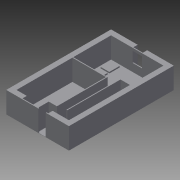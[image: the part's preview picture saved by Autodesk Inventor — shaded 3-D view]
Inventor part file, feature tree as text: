
AUTODESK INVENTOR PART (.ipt)
format: ipt  version: 2014 (Build 180170000, 170)  size: 305,664 bytes
history: native  units: in
note: dims shown in document units (in); Inventor stores cm internally (conversion verified against a paired STEP export)
features: extrude x7, sketch x7, projected_geometry x2
ambient origin geometry x8: Origin, YZ Plane, XZ Plane, XY Plane, X Axis, Y Axis, Z Axis, Center Point
bodies: Solid1 (feature_tree)
feature tree (16):
  extrude  "Extrusion1"  Depth=480.315in
  extrude  "Extrusion2"  Depth=456.6929in
  extrude  "Extrusion6"  Depth=118.1102in
  extrude  "Extrusion7"  Depth=98.4252in
  extrude  "Pallets"  Depth=433.0709in
  extrude  "Furniture"  Depth=157.4803in
  extrude  "Instrumentation"  Depth=3.937in
  sketch  "Sketch1"  dims[d0=287.4016in d1=480.315in]
  sketch  "Sketch2"  dims[d2=240.1575in d4=456.6929in]
  projected_geometry  "Projected Loop1"
  sketch  "Sketch3"  dims[d5=74.8031in d6=118.1102in]
  sketch  "Sketch4"  dims[d7=98.4252in d8=98.4252in]
  sketch  "Sketch5"  dims[d9=480.315in d10=433.0709in]
  sketch  "Sketch6"  dims[d11=3.937in d12=157.4803in]
  projected_geometry  "Projected Loop2"
  sketch  "Sketch7"  dims[d14=3.937in d16=3.937in d17=3.937in d18=3.937in d19=7.874in d20=3.937in d22=47.2441in d23=255.9055in d24=3.937in d25=3.937in d26=47.2441in d27=149.6063in d28=3.937in d29=248.0315in d30=96.0in d31=0.0in d32=1.0in d33=0.0in d34=82.6772in d35=78.7402in d36=82.6772in d37=78.7402in d38=12.0in d39=12.0in d40=82.6772in d41=82.6772in d43=12.0in d44=12.0in d45=12.0in d51=23.622in d52=23.622in d53=12.0in d54=12.0in d56=86.6142in d59=23.622in d60=17.867in d61=17.867in d62=17.867in d63=12.0in d65=12.0in d66=12.0in d73=6.0in d74=10.0in d75=10.0in d76=6.0in d77=6.0in d78=0.0in d79=39.3701in d80=47.2441in d81=47.2441in d82=7.874in d83=11.811in d84=11.811in d85=6.0in d86=0.0in d87=62.9921in d88=35.4331in d89=35.4331in d90=39.3701in d91=27.5591in d92=31.4961in d93=106.2992in d94=43.3071in d95=27.5591in d98=31.4961in d99=6.0in d100=0.0in d101=62.9921in d102=3.937in d103=1.0in d104=0.0in d107=12.0in d108=12.0in d109=45.0deg d110=6.0in d111=36.0in d112=1.0in d113=0.0in d116=12.0in d117=12.0in d118=6.0in]
